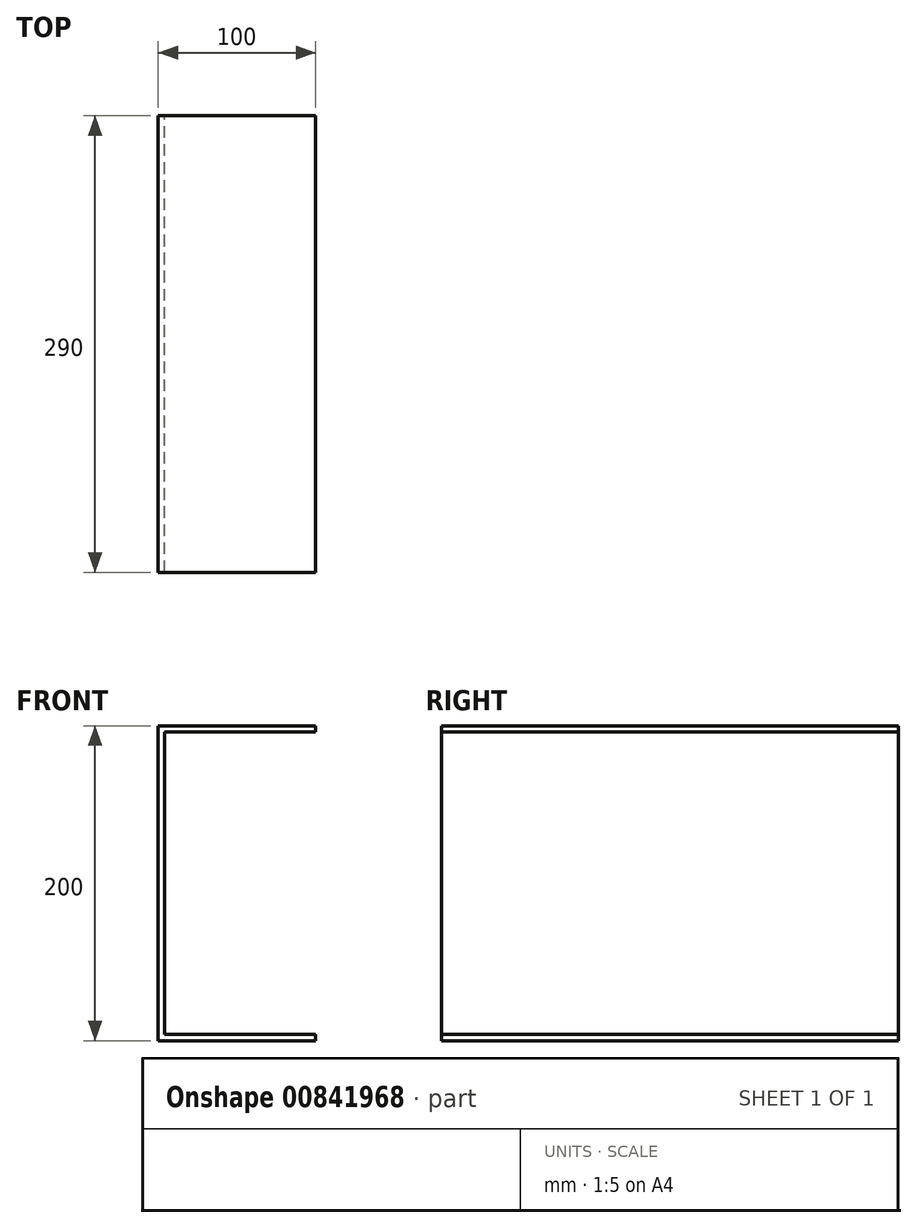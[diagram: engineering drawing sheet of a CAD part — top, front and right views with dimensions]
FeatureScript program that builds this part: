
annotation { "Feature Type Name" : "Feature", "Feature Type Description" : "" }
export const myFeature = defineFeature(function(context is Context, id is Id, definition is map)
    precondition{}
    {
        {
            var Q0;
            Q0=qCreatedBy(makeId("Front.planeOp"),FACE);
            var sketch = newSketch(context, id + "F0", { "sketchPlane" : qUnion([Q0])});
            skLineSegment(sketch, "E0", {"start": v(43.8, 100) * mm, "end": v(-56.2, 100) * mm});
            skLineSegment(sketch, "E1", {"start": v(-56.2, 100) * mm, "end": v(-56.2, -100) * mm});
            skLineSegment(sketch, "E2", {"start": v(-56.2, -100) * mm, "end": v(43.8, -100) * mm});
            skLineSegment(sketch, "E3.0", {"start": v(-52.2, -96) * mm, "end": v(43.8, -96) * mm});
            skLineSegment(sketch, "E3.1", {"start": v(-52.2, 96) * mm, "end": v(-52.2, -96) * mm});
            skLineSegment(sketch, "E3.2", {"start": v(43.8, 96) * mm, "end": v(-52.2, 96) * mm});
            skLineSegment(sketch, "E4", {"start": v(43.8, 96) * mm, "end": v(43.8, 100) * mm});
            skLineSegment(sketch, "E5", {"start": v(43.8, -100) * mm, "end": v(43.8, -96) * mm});
            skSolve(sketch);
        }
        {
            var Q0;
            Q0=makeQuery(id+"F0.imprint","IMPRINT",FACE,{"disambiguationData":[TD([[makeQuery(id+"F0.imprint","IMPRINT",EDGE,{"derivedFrom":sQuery(id+"F0.wireOp",EDGE,"E0")}),1.0]])]});
            extrude(context, id + "F1", {"entities" : qUnion([Q0]), "endBound" : BoundingType.SYMMETRIC, "depth" : 290 * mm, "offsetDistance" : 25 * mm});
        }
    });
